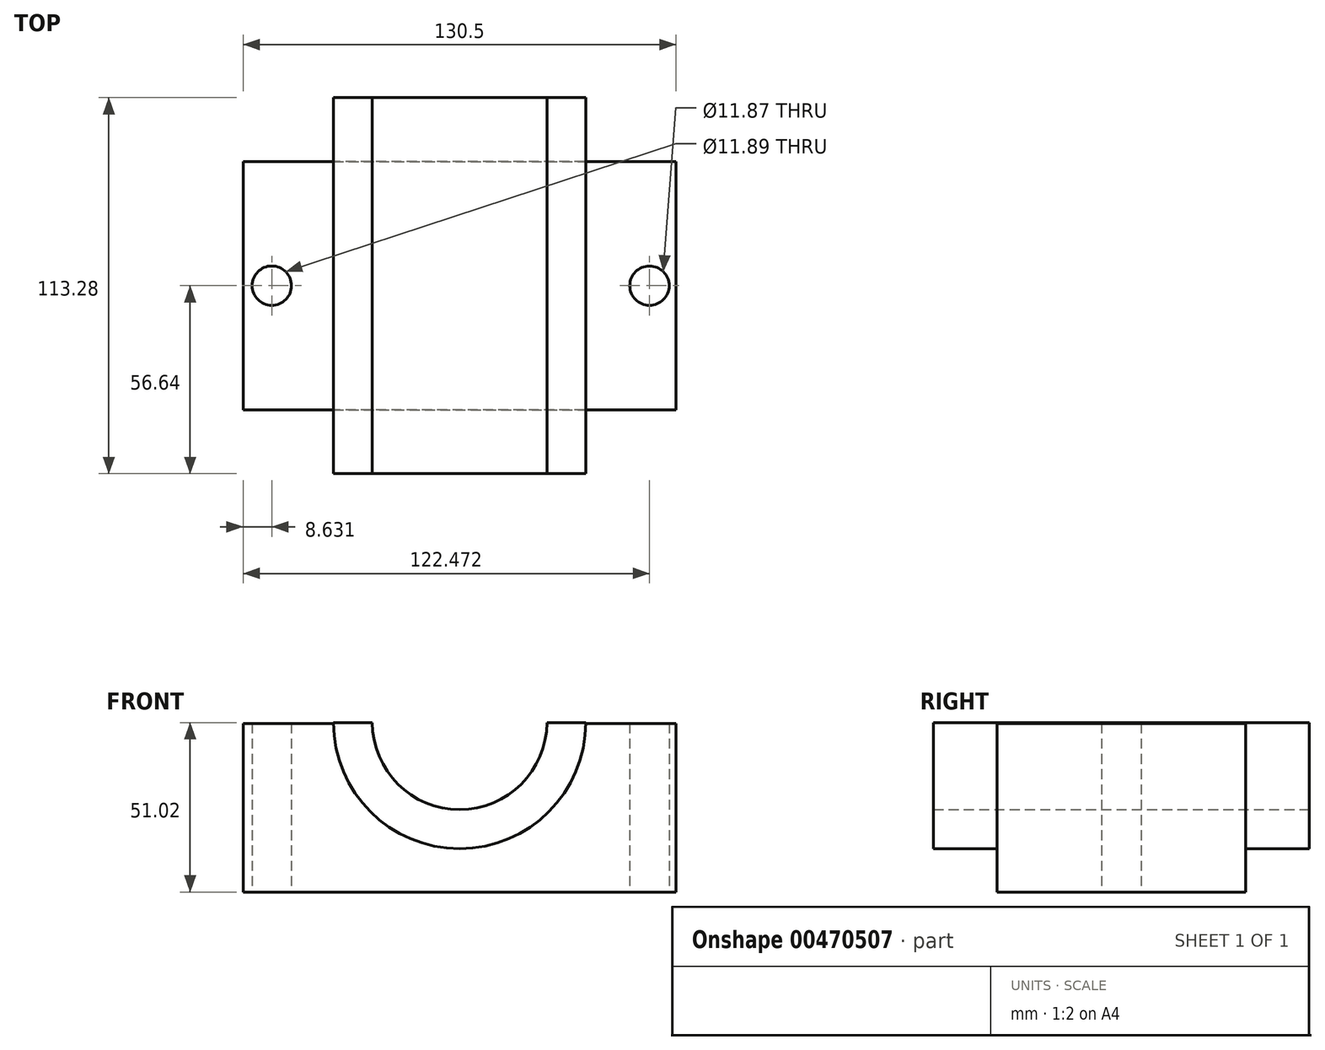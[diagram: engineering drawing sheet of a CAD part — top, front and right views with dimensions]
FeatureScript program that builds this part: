
annotation { "Feature Type Name" : "Feature", "Feature Type Description" : "" }
export const myFeature = defineFeature(function(context is Context, id is Id, definition is map)
    precondition{}
    {
        {
            var Q0;
            Q0=qCreatedBy(makeId("Top.planeOp"),FACE);
            var sketch = newSketch(context, id + "F0", { "sketchPlane" : qUnion([Q0])});
            skLineSegment(sketch, "E0.bottom", {"start": v(65.25, -37.45) * mm, "end": v(-65.25, -37.45) * mm});
            skLineSegment(sketch, "E0.top", {"start": v(65.25, 37.45) * mm, "end": v(-65.25, 37.45) * mm});
            skLineSegment(sketch, "E0.left", {"start": v(65.25, -37.45) * mm, "end": v(65.25, 37.45) * mm});
            skLineSegment(sketch, "E0.right", {"start": v(-65.25, -37.45) * mm, "end": v(-65.25, 37.45) * mm});
            skPoint(sketch, "E0.middle", {"position": v(0, 0) * mm});
            skCircle(sketch, "E1", {"center": v(57.22, 0) * mm, "radius": 5.94 * mm});
            skCircle(sketch, "E2", {"center": v(-56.62, 0) * mm, "radius": 5.94 * mm});
            skSolve(sketch);
        }
        {
            var Q0;
            Q0 = qSketchRegion(id + "F0", true);
            extrude(context, id + "F1", {"entities" : qUnion([Q0]), "depth" : 50.8 * mm});
        }
        {
            var Q0;
            Q0=qCreatedBy(makeId("Front.planeOp"),FACE);
            var sketch = newSketch(context, id + "F2", { "sketchPlane" : qUnion([Q0])});
            skArc(sketch, "E3", {"start": v(-38.05, 51) * mm, "mid": v(0, 13.05) * mm, "end": v(38.05, 51.02) * mm});
            skArc(sketch, "E4", {"start": v(-26.31, 51) * mm, "mid": v(0, 24.79) * mm, "end": v(26.31, 51.02) * mm});
            skLineSegment(sketch, "E5", {"start": v(38.05, 51.02) * mm, "end": v(26.31, 51.02) * mm});
            skLineSegment(sketch, "E6", {"start": v(-38.05, 51) * mm, "end": v(-26.31, 51) * mm});
            skSolve(sketch);
        }
        {
            var Q0;
            Q0 = qSketchRegion(id + "F2", true);
            extrude(context, id + "F3", {"entities" : qUnion([Q0]), "operationType" : NewBodyOperationType.ADD, "endBound" : BoundingType.SYMMETRIC, "depth" : 113.28 * mm});
        }
        {
            var Q0;
            {var subQ0=sQuery(id+"F0.wireOp",EDGE,"E0.top");Q0=makeQuery(id+"F3.boolean.opBoolean","SPLIT",FACE,{"disambiguationData":[TD([makeQuery(id+"F3.opExtrude","SWEPT_FACE",FACE,{"disambiguationData":[OSD([sQuery(id+"F2.wireOp",EDGE,"E4")])]})])],"derivedFrom":makeQuery(id+"F1.opExtrude","SWEPT_FACE",FACE,{"disambiguationData":[OSD([subQ0])]})});}
            extrude(context, id + "F4", {"entities" : qUnion([Q0]), "operationType" : NewBodyOperationType.REMOVE, "endBound" : BoundingType.SYMMETRIC, "oppositeDirection" : true, "depth" : 222.5 * mm});
        }
    });
